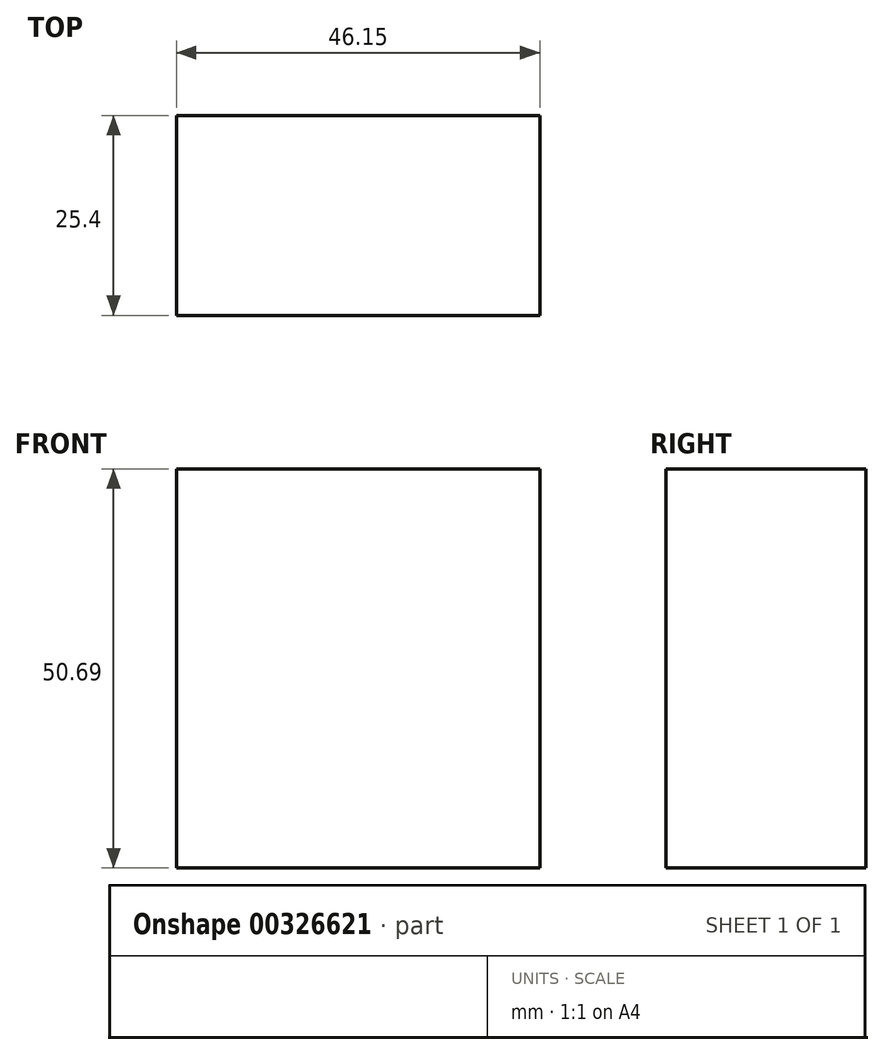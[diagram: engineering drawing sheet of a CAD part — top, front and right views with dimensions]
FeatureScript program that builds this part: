
annotation { "Feature Type Name" : "Feature", "Feature Type Description" : "" }
export const myFeature = defineFeature(function(context is Context, id is Id, definition is map)
    precondition{}
    {
        {
            var Q0;
            Q0=qCreatedBy(makeId("Front.planeOp"),FACE);
            var sketch = newSketch(context, id + "F0", { "sketchPlane" : qUnion([Q0])});
            skLineSegment(sketch, "E0.bottom", {"start": v(35.84, 0) * mm, "end": v(41.2, 0) * mm});
            skLineSegment(sketch, "E0.top", {"start": v(35.84, 0) * mm, "end": v(41.2, 0) * mm});
            skLineSegment(sketch, "E0.left", {"start": v(35.84, 0) * mm, "end": v(35.84, 0) * mm});
            skLineSegment(sketch, "E0.right", {"start": v(41.2, 0) * mm, "end": v(41.2, 0) * mm});
            skLineSegment(sketch, "E1.bottom", {"start": v(35.84, -17.1) * mm, "end": v(41.2, -17.1) * mm});
            skLineSegment(sketch, "E1.top", {"start": v(35.84, -14.37) * mm, "end": v(41.2, -14.37) * mm});
            skLineSegment(sketch, "E1.left", {"start": v(35.84, -17.1) * mm, "end": v(35.84, -14.37) * mm});
            skLineSegment(sketch, "E1.right", {"start": v(41.2, -17.1) * mm, "end": v(41.2, -14.37) * mm});
            skLineSegment(sketch, "E2.bottom", {"start": v(64.23, 36.32) * mm, "end": v(18.08, 36.32) * mm});
            skLineSegment(sketch, "E2.top", {"start": v(64.23, -14.37) * mm, "end": v(18.08, -14.37) * mm});
            skLineSegment(sketch, "E2.left", {"start": v(64.23, 36.32) * mm, "end": v(64.23, -14.37) * mm});
            skLineSegment(sketch, "E2.right", {"start": v(18.08, 36.32) * mm, "end": v(18.08, -14.37) * mm});
            skSolve(sketch);
        }
        {
            var Q0;
            Q0=makeQuery(id+"F0.imprint","IMPRINT",FACE,{"disambiguationData":[TD([[makeQuery(id+"F0.imprint","IMPRINT",EDGE,{"derivedFrom":sQuery(id+"F0.wireOp",EDGE,"E2.bottom")}),1.0]])]});
            extrude(context, id + "F1", {"entities" : qUnion([Q0]), "depth" : 25.4 * mm});
        }
    });
